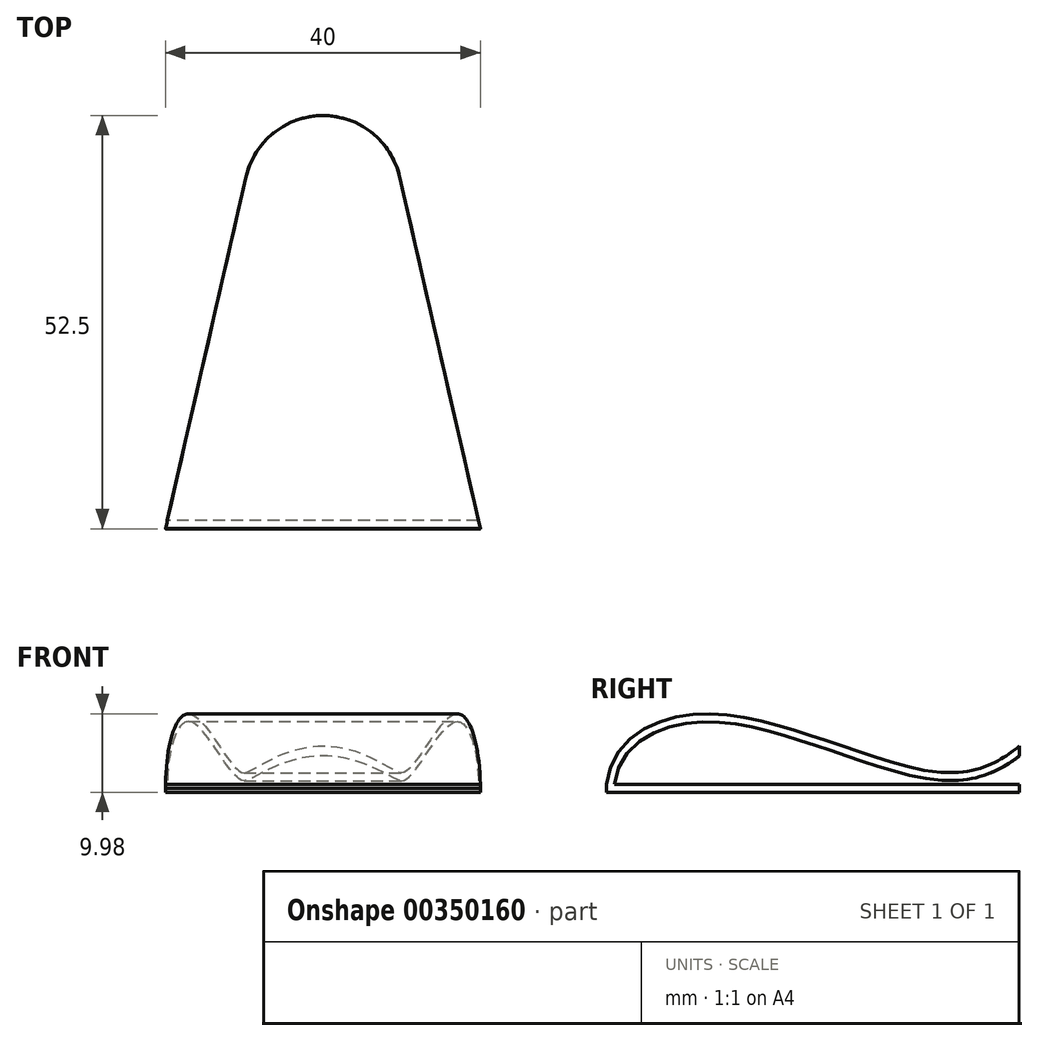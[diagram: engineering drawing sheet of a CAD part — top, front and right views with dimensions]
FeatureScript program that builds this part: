
annotation { "Feature Type Name" : "Feature", "Feature Type Description" : "" }
export const myFeature = defineFeature(function(context is Context, id is Id, definition is map)
    precondition{}
    {
        {
            var Q0;
            Q0=qCreatedBy(makeId("Top.planeOp"),FACE);
            var sketch = newSketch(context, id + "F0", { "sketchPlane" : qUnion([Q0])});
            skLineSegment(sketch, "E0.bottom", {"start": v(30, 42.5) * mm, "end": v(-30, 42.5) * mm});
            skLineSegment(sketch, "E0.top", {"start": v(30, -42.5) * mm, "end": v(-30, -42.5) * mm});
            skLineSegment(sketch, "E0.left", {"start": v(30, 42.5) * mm, "end": v(30, -42.5) * mm});
            skLineSegment(sketch, "E0.right", {"start": v(-30, 42.5) * mm, "end": v(-30, -42.5) * mm});
            skPoint(sketch, "E0.middle", {"position": v(0, 0) * mm});
            skLineSegment(sketch, "E1", {"start": v(0, -42.5) * mm, "end": v(0, 0) * mm});
            skArc(sketch, "E2", {"start": v(9.75, 2.23) * mm, "mid": v(0, 10) * mm, "end": v(-9.75, 2.23) * mm});
            skLineSegment(sketch, "E3", {"start": v(9.75, 2.23) * mm, "end": v(20, -42.5) * mm});
            skLineSegment(sketch, "E4.MirrorCS", {"start": v(-9.75, 2.23) * mm, "end": v(-20, -42.5) * mm});
            skLineSegment(sketch, "E5", {"start": v(-20, -42.5) * mm, "end": v(20, -42.5) * mm});
            skLineSegment(sketch, "E6", {"start": v(19.77, -41.5) * mm, "end": v(-19.77, -41.5) * mm});
            skLineSegment(sketch, "E7", {"start": v(-19.77, -41.5) * mm, "end": v(-19.77, -41.5) * mm});
            skLineSegment(sketch, "E8", {"start": v(-19.77, -41.5) * mm, "end": v(-20, -42.5) * mm});
            skLineSegment(sketch, "E9", {"start": v(19.77, -41.5) * mm, "end": v(20, -42.5) * mm});
            skSolve(sketch);
        }
        {
            var Q0;
            Q0=makeQuery(id+"F0.imprint","IMPRINT",FACE,{"disambiguationData":[TD([[makeQuery(id+"F0.imprint","IMPRINT",EDGE,{"derivedFrom":sQuery(id+"F0.wireOp",EDGE,"E0.bottom")}),1.0]])]});
            var Q1;
            {var subQ5=sQuery(id+"F0.wireOp",EDGE,"E8");Q1=makeQuery(id+"F0.imprint","IMPRINT",FACE,{"disambiguationData":[TD([[makeQuery(id+"F0.imprint","IMPRINT",EDGE,{"derivedFrom":subQ5}),1.0]])]});}
            var Q2;
            {var subQ5=sQuery(id+"F0.wireOp",EDGE,"E9");Q2=makeQuery(id+"F0.imprint","IMPRINT",FACE,{"disambiguationData":[TD([[makeQuery(id+"F0.imprint","IMPRINT",EDGE,{"derivedFrom":subQ5}),-1.0]])]});}
            var Q3;
            Q3=makeQuery(id+"F0.imprint","IMPRINT",FACE,{"disambiguationData":[TD([[makeQuery(id+"F0.imprint","IMPRINT",EDGE,{"derivedFrom":sQuery(id+"F0.wireOp",EDGE,"E2")}),1.0]])]});
            extrude(context, id + "F1", {"entities" : qUnion([Q0, Q1, Q2, Q3]), "depth" : 1 * mm});
        }
        {
            var Q0;
            Q0=qCreatedBy(makeId("Right.planeOp"),FACE);
            var sketch = newSketch(context, id + "F2", { "sketchPlane" : qUnion([Q0])});
            skFitSpline(sketch, "E10", {"points": [v(-42.47, 0) * mm, v(-30, 9.95) * mm, v(1.45, 2.44) * mm, v(10.18, 6) * mm], "startDerivative": vector(-1.58, 56.7) * mm, "endDerivative": vector(18.02, 14.16) * mm});
            skSolve(sketch);
        }
        {
            var Q0;
            {var subQ5=sQuery(id+"F0.wireOp",EDGE,"E9");Q0=makeQuery(id+"F0.imprint","IMPRINT",FACE,{"disambiguationData":[TD([[makeQuery(id+"F0.imprint","IMPRINT",EDGE,{"derivedFrom":subQ5}),-1.0]])]});}
            var Q1;
            {var subQ5=sQuery(id+"F0.wireOp",EDGE,"E8");Q1=makeQuery(id+"F0.imprint","IMPRINT",FACE,{"disambiguationData":[TD([[makeQuery(id+"F0.imprint","IMPRINT",EDGE,{"derivedFrom":subQ5}),1.0]])]});}
            var Q2;
            Q2=sQuery(id+"F2.wireOp",EDGE,"E10");
            sweep(context, id + "F3", {"operationType" : NewBodyOperationType.ADD, "profiles" : qUnion([Q0, Q1]), "path" : qUnion([Q2])});
        }
        {
            var Q0;
            Q0=makeQuery(id+"F0.imprint","IMPRINT",FACE,{"disambiguationData":[TD([[makeQuery(id+"F0.imprint","IMPRINT",EDGE,{"derivedFrom":sQuery(id+"F0.wireOp",EDGE,"E2")}),1.0]])]});
            var Q1;
            {var subQ5=sQuery(id+"F0.wireOp",EDGE,"E9");Q1=makeQuery(id+"F0.imprint","IMPRINT",FACE,{"disambiguationData":[TD([[makeQuery(id+"F0.imprint","IMPRINT",EDGE,{"derivedFrom":subQ5}),-1.0]])]});}
            var Q2;
            {var subQ5=sQuery(id+"F0.wireOp",EDGE,"E8");Q2=makeQuery(id+"F0.imprint","IMPRINT",FACE,{"disambiguationData":[TD([[makeQuery(id+"F0.imprint","IMPRINT",EDGE,{"derivedFrom":subQ5}),1.0]])]});}
            extrude(context, id + "F4", {"entities" : qUnion([Q0, Q1, Q2]), "operationType" : NewBodyOperationType.INTERSECT, "depth" : 25 * mm});
        }
    });
